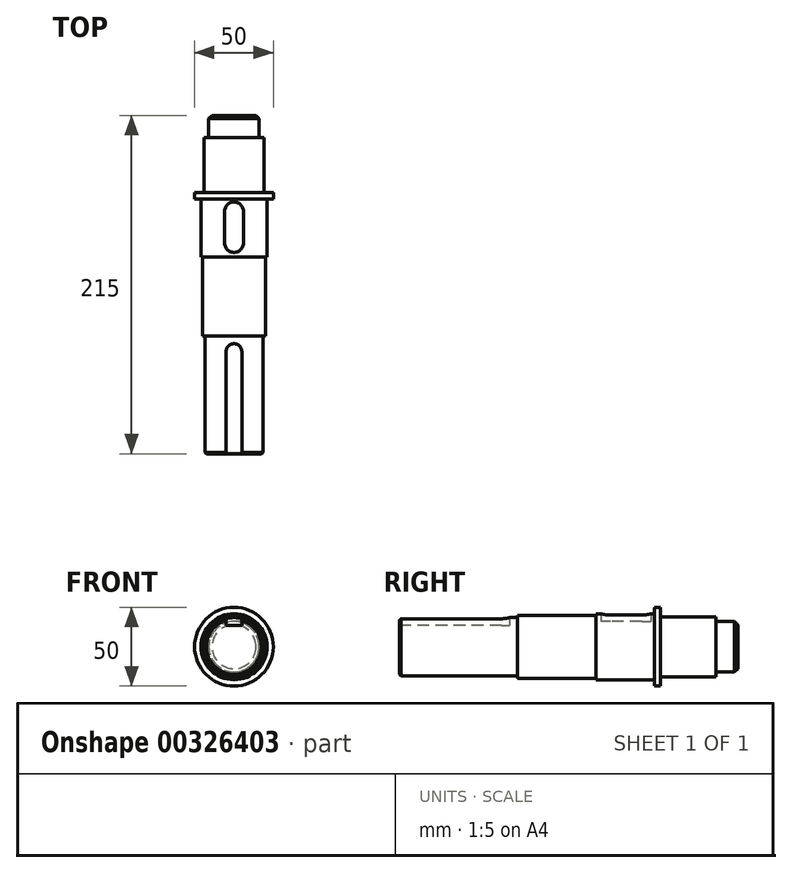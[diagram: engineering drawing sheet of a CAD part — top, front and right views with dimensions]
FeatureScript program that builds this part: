
annotation { "Feature Type Name" : "Feature", "Feature Type Description" : "" }
export const myFeature = defineFeature(function(context is Context, id is Id, definition is map)
    precondition{}
    {
        {
            var Q0;
            Q0=qCreatedBy(makeId("Right.planeOp"),FACE);
            var sketch = newSketch(context, id + "F0", { "sketchPlane" : qUnion([Q0])});
            skLineSegment(sketch, "E0", {"start": v(0, 0) * mm, "end": v(0, 18.5) * mm});
            skLineSegment(sketch, "E1", {"start": v(0, 18.5) * mm, "end": v(75, 18.5) * mm});
            skLineSegment(sketch, "E2", {"start": v(75, 18.5) * mm, "end": v(75, 20) * mm});
            skLineSegment(sketch, "E3", {"start": v(75, 20) * mm, "end": v(125, 20) * mm});
            skLineSegment(sketch, "E4", {"start": v(125, 20) * mm, "end": v(125, 21) * mm});
            skLineSegment(sketch, "E5", {"start": v(125, 21) * mm, "end": v(162, 21) * mm});
            skLineSegment(sketch, "E6", {"start": v(162, 21) * mm, "end": v(162, 25) * mm});
            skLineSegment(sketch, "E7", {"start": v(162, 25) * mm, "end": v(166, 25) * mm});
            skLineSegment(sketch, "E8", {"start": v(166, 25) * mm, "end": v(166, 19) * mm});
            skLineSegment(sketch, "E9", {"start": v(166, 19) * mm, "end": v(201, 19) * mm});
            skLineSegment(sketch, "E10", {"start": v(201, 19) * mm, "end": v(201, 16) * mm});
            skLineSegment(sketch, "E11", {"start": v(201, 16) * mm, "end": v(215, 16) * mm});
            skLineSegment(sketch, "E12", {"start": v(215, 16) * mm, "end": v(215, 0) * mm});
            skLineSegment(sketch, "E13", {"start": v(215, 0) * mm, "end": v(0, 0) * mm});
            skLineSegment(sketch, "E14", {"start": v(-17.81, 0) * mm, "end": v(227.9, 0) * mm, "construction": true});
            skSolve(sketch);
        }
        {
            var Q0;
            Q0=makeQuery(id+"F0.imprint","IMPRINT",FACE,{"disambiguationData":[TD([[makeQuery(id+"F0.imprint","IMPRINT",EDGE,{"derivedFrom":sQuery(id+"F0.wireOp",EDGE,"E0")}),-1.0]])]});
            var Q1;
            Q1=sQuery(id+"F0.wireOp",EDGE,"E14");
            revolve(context, id + "F1", {"entities" : qUnion([Q0]), "axis" : qUnion([Q1]), "revolveType" : RevolveType.FULL});
        }
        {
            var Q0;
            Q0=makeQuery(id+"F1.opRevolve","SWEPT_EDGE",EDGE,{"disambiguationData":[OSD([sQuery(id+"F0.wireOp",EDGE,"E0"),sQuery(id+"F0.wireOp",EDGE,"E1")])]});
            chamfer(context, id + "F2", {"entities" : qUnion([Q0]), "width" : 1 * mm, "tangentPropagation" : true});
        }
        {
            var Q0;
            Q0=makeQuery(id+"F1.opRevolve","SWEPT_EDGE",EDGE,{"disambiguationData":[OSD([sQuery(id+"F0.wireOp",EDGE,"E11"),sQuery(id+"F0.wireOp",EDGE,"E12")])]});
            chamfer(context, id + "F3", {"entities" : qUnion([Q0]), "width" : 2 * mm, "tangentPropagation" : true});
        }
        {
            var Q0;
            Q0=qCreatedBy(makeId("Top.planeOp"),FACE);
            cPlane(context, id + "F4", {"entities" : qUnion([Q0]), "cplaneType" : CPlaneType.OFFSET, "offset" : 13.5 * mm, "width" : 150 * mm, "height" : 150 * mm});
        }
        {
            var Q0;
            Q0=qCreatedBy(id+"F4.planeOp",FACE);
            var sketch = newSketch(context, id + "F5", { "sketchPlane" : qUnion([Q0])});
            skLineSegment(sketch, "E15", {"start": v(5, 65) * mm, "end": v(5, -5) * mm});
            skLineSegment(sketch, "E16", {"start": v(5, -5) * mm, "end": v(0, -5) * mm});
            skArc(sketch, "E17", {"start": v(5, 65) * mm, "mid": v(0, 70) * mm, "end": v(-5, 65) * mm});
            skLineSegment(sketch, "E18.MirrorCS", {"start": v(-5, 65) * mm, "end": v(-5, -5) * mm});
            skLineSegment(sketch, "E19", {"start": v(0, -5) * mm, "end": v(-5, -5) * mm});
            skLineSegment(sketch, "E20", {"start": v(-23.84, 70) * mm, "end": v(25.42, 70) * mm, "construction": true});
            skSolve(sketch);
        }
        {
            var Q0;
            Q0=makeQuery(id+"F5.imprint","IMPRINT",FACE,{"disambiguationData":[TD([[makeQuery(id+"F5.imprint","IMPRINT",EDGE,{"derivedFrom":sQuery(id+"F5.wireOp",EDGE,"E15")}),-1.0]])]});
            extrude(context, id + "F6", {"entities" : qUnion([Q0]), "operationType" : NewBodyOperationType.REMOVE, "endBound" : BoundingType.THROUGH_ALL, "depth" : 25 * mm});
        }
        {
            var Q0;
            Q0=qCreatedBy(makeId("Top.planeOp"),FACE);
            cPlane(context, id + "F7", {"entities" : qUnion([Q0]), "cplaneType" : CPlaneType.OFFSET, "offset" : 16 * mm, "width" : 150 * mm, "height" : 150 * mm});
        }
        {
            var Q0;
            Q0=qCreatedBy(id+"F7.planeOp",FACE);
            var sketch = newSketch(context, id + "F8", { "sketchPlane" : qUnion([Q0])});
            skLineSegment(sketch, "E21", {"start": v(6, 154) * mm, "end": v(6, 134) * mm});
            skArc(sketch, "E22", {"start": v(6, 154) * mm, "mid": v(0, 160) * mm, "end": v(-6, 154) * mm});
            skArc(sketch, "E23", {"start": v(6, 134) * mm, "mid": v(0, 128) * mm, "end": v(-6, 134) * mm});
            skLineSegment(sketch, "E24", {"start": v(-6, 154) * mm, "end": v(-6, 134) * mm});
            skLineSegment(sketch, "E25", {"start": v(-18, 160) * mm, "end": v(18, 160) * mm, "construction": true});
            skLineSegment(sketch, "E26", {"start": v(18, 128) * mm, "end": v(-18, 128) * mm, "construction": true});
            skPoint(sketch, "E27", {"position": v(0, 128) * mm});
            skSolve(sketch);
        }
        {
            var Q0;
            Q0 = qSketchRegion(id + "F8", true);
            extrude(context, id + "F9", {"entities" : qUnion([Q0]), "operationType" : NewBodyOperationType.REMOVE, "endBound" : BoundingType.THROUGH_ALL, "depth" : 25 * mm});
        }
    });
